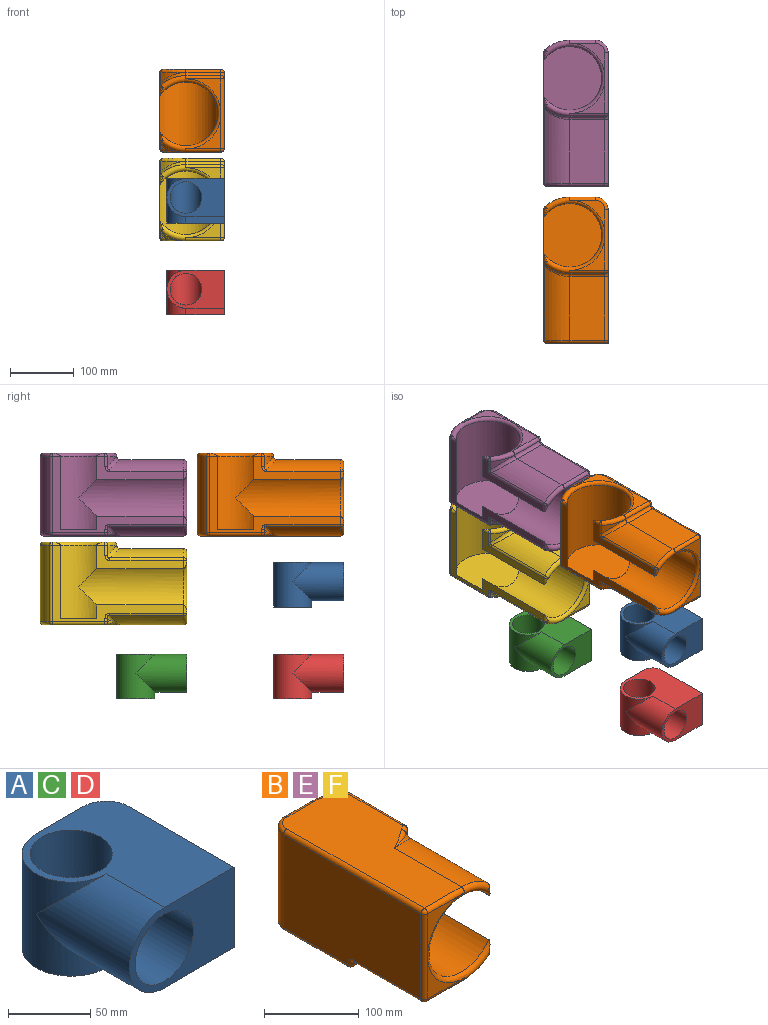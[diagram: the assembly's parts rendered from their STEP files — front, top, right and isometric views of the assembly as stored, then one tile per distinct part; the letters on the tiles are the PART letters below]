
ASSEMBLY  parts=6 mates=11
PART A: 12 faces, bbox 90x110x70 mm
  f0: cylinder r=30mm len=70mm, axis (0,0,-1), area 4797.3mm2, adj f1,f2,f3,f6,f7
  f1: cylinder r=30mm len=80mm, axis (0,1,0), area 5739.8mm2, adj f0,f2,f4,f5
  f2: plane 110x90mm, normal (0,0,1), area 5964.4mm2, adj f0,f1,f4,f7,f8,f9,f11
  f3: plane 90x60mm, normal (0,0,-1), area 2964.4mm2, adj f0,f6,f7,f8,f9,f11
  f4: plane 90x60mm, normal (0,-1,0), area 3050.2mm2, adj f1,f2,f5,f8,f10
  f5: plane 60x50mm, normal (0,0,-1), area 3000mm2, adj f1,f4,f6,f8
  f6: plane 60x10mm, normal (0,-1,0), area 600mm2, adj f0,f3,f5,f8
  f7: plane 70x40mm, normal (0,1,0), area 2800mm2, adj f0,f2,f3,f11
  f8: plane 90x70mm, normal (1,0,0), area 5800mm2, adj f2,f3,f4,f5,f6,f11
  f9: cylinder r=25mm len=70mm, axis (0,0,-1), area 8495.6mm2, adj f2,f3,f10
  f10: cylinder r=25mm len=80mm, axis (0,-1,0), area 10066.4mm2, adj f4,f9
  f11: cylinder r=20mm len=70mm, axis (0,0,-1), area 2199.1mm2, adj f2,f3,f7,f8
PART B: 61 faces, bbox 118.2x234.9x135 mm
  f0: plane 220x91mm, normal (0,0,1), area 15826.8mm2, adj f9,f38,f43,f44,f46,f49,f51,f52
  f1: plane 55x55mm, normal (0,0,-1), area 600.9mm2, adj f29,f30,f33,f60
  f2: plane 55x55mm, normal (0,0,-1), area 649.2mm2, adj f24,f29,f30
  f3: plane 55x55mm, normal (0,-1,0), area 649.2mm2, adj f34,f40,f44
  f4: cylinder r=60mm len=7.3mm, axis (0,0,-1), area 26.6mm2, adj f52,f53,f57
  f5: cylinder r=60mm len=39.27mm, axis (0,0,-1), area 339.5mm2, adj f21,f22,f29
  f6: cylinder r=60mm len=115.86mm, axis (0,1,0), area 4621mm2, adj f12,f21,f32,f40
  f7: cylinder r=50mm len=115mm, axis (0,0,-1), area 20203.4mm2, adj f15,f16,f17,f18,f29
  f8: cylinder r=60mm len=120mm, axis (0,0,-1), area 5137.8mm2, adj f13,f29,f45,f46
  f9: cylinder r=60mm len=115.86mm, axis (0,1,0), area 4621mm2, adj f0,f40,f53,f54
  f10: plane 55x55mm, normal (0,-1,0), area 649.2mm2, adj f34,f35,f40
  f11: plane 205x120mm, normal (-1,0,0), area 23521.5mm2, adj f20,f26,f30,f34,f38,f59
  f12: plane 100x55mm, normal (0,0,-1), area 5500mm2, adj f6,f19,f26,f35
  f13: plane 120x40mm, normal (0,1,0), area 4800mm2, adj f8,f33,f43,f59
  f14: cylinder r=50mm len=41mm, axis (0,0,-1), area 513.9mm2, adj f15,f16,f18
  f15: plane 100x91mm, normal (0,0,-1), area 7503.9mm2, adj f7,f14,f18
  f16: cylinder r=50mm len=165mm, axis (0,-1,0), area 33378.3mm2, adj f7,f14,f17,f18,f40
  f17: plane 136.38x36.38mm, normal (1,0,0), area 2082.1mm2, adj f7,f16,f22,f27,f28,f32,f41
  f18: plane 206.58x120mm, normal (1,0,0), area 3794.2mm2, adj f7,f14,f15,f16,f37,f45,f47,f51
  f19: cylinder r=5mm len=55mm, axis (-1,0,0), area 432mm2, adj f12,f20,f21,f24
  f20: torus R=10mm, axis (-1,0,0), area 84.1mm2, adj f11,f19,f25,f26
  f21: bspline ~51.65x23.96mm, area 321.1mm2, adj f5,f6,f19,f27
  f22: cylinder r=5mm len=15.86mm, axis (0,0,-1), area 68mm2, adj f5,f17,f23,f27
  f23: sphere r=5mm, area 13.6mm2, adj f22,f28,f29
  f24: cylinder r=5mm len=55mm, axis (-1,0,0), area 432mm2, adj f2,f19,f25,f29
  f25: sphere r=5mm, area 39.3mm2, adj f20,f24,f30
  f26: cylinder r=5mm len=100mm, axis (0,-1,0), area 785.4mm2, adj f11,f12,f20,f31
  f27: bspline ~9.27x8.4mm, area 34.5mm2, adj f17,f21,f22,f32
  f28: cylinder r=5mm len=12.96mm, axis (0,1,0), area 50.9mm2, adj f17,f23,f29
  f29: torus R=55mm, axis (0,0,1), area 2610.7mm2, adj f1,f2,f5,f7,f8,f23,f24,f28
  f30: cylinder r=5mm len=95mm, axis (0,-1,0), area 746.1mm2, adj f1,f2,f11,f25,f60
  f31: sphere r=5mm, area 25mm2, adj f26,f34,f35
  f32: cylinder r=5mm len=115.86mm, axis (0,1,0), area 496.6mm2, adj f6,f17,f27,f36
  f33: cylinder r=5mm len=40mm, axis (-1,0,0), area 314.2mm2, adj f1,f13,f29,f60
  f34: cylinder r=5mm len=110mm, axis (0,0,1), area 863.9mm2, adj f3,f10,f11,f31,f39
  f35: cylinder r=5mm len=55mm, axis (1,0,0), area 432mm2, adj f10,f12,f31,f40
  f36: sphere r=5mm, area 27.9mm2, adj f32,f40,f41
  f37: cylinder r=5mm len=12.96mm, axis (0,1,0), area 50.9mm2, adj f18,f29,f42
  f38: cylinder r=5mm len=205mm, axis (0,1,0), area 1610.1mm2, adj f0,f11,f39,f58
  f39: sphere r=5mm, area 53.5mm2, adj f34,f38,f44
  f40: torus R=55mm, axis (0,-1,0), area 2610.7mm2, adj f3,f6,f9,f10,f16,f35,f36,f41
  f41: cylinder r=5mm len=12.96mm, axis (0,0,-1), area 50.9mm2, adj f17,f36,f40
  f42: sphere r=5mm, area 21.4mm2, adj f29,f37,f45
  f43: cylinder r=5mm len=40mm, axis (1,0,0), area 314.2mm2, adj f0,f13,f46,f58
  f44: cylinder r=5mm len=55mm, axis (1,0,0), area 432mm2, adj f0,f3,f39,f40
  f45: cylinder r=5mm len=120mm, axis (0,0,-1), area 514.3mm2, adj f8,f18,f42,f48
  f46: torus R=55mm, axis (0,0,1), area 326.1mm2, adj f0,f8,f43,f48
  f47: cylinder r=5mm len=12.96mm, axis (0,0,-1), area 50.9mm2, adj f18,f40,f50
  f48: sphere r=5mm, area 21.4mm2, adj f45,f46,f51
  f49: bspline ~35.02x20.17mm, area 89.6mm2, adj f0,f52,f53
  f50: sphere r=5mm, area 21.4mm2, adj f40,f47,f54
  f51: cylinder r=5mm len=83.16mm, axis (0,-1,0), area 653.2mm2, adj f0,f18,f48,f55
  f52: torus R=55mm, axis (0,0,1), area 69.2mm2, adj f0,f4,f49,f55
  f53: bspline ~45.78x23.96mm, area 192mm2, adj f4,f9,f49,f56
  f54: cylinder r=5mm len=115.86mm, axis (0,1,0), area 496.6mm2, adj f9,f18,f50,f56
  f55: sphere r=5mm, area 21.4mm2, adj f51,f52,f57
  f56: bspline ~9.27x8.4mm, area 34.5mm2, adj f18,f53,f54,f57
  f57: cylinder r=5mm len=5.86mm, axis (0,0,-1), area 25.1mm2, adj f4,f18,f55,f56
  f58: torus R=15mm, axis (0,0,1), area 224.3mm2, adj f0,f38,f43,f59
  f59: cylinder r=20mm len=120mm, axis (0,0,-1), area 3769.9mm2, adj f11,f13,f58,f60
  f60: torus R=15mm, axis (0,0,1), area 224.3mm2, adj f1,f30,f33,f59
PART C: same geometry as A
PART D: same geometry as A
PART E: same geometry as B
PART F: same geometry as B
PLACE A rot(axis=(-0.07,-0.3,-0.95),0deg) t=(344.34,-371.74,253.96)mm
PLACE B rot(axis=(0,1,0),180deg) t=(262.34,-281.74,385.51)mm
PLACE C rot(axis=(-0.07,-0.3,-0.95),0deg) t=(344.34,-125.03,109.89)mm
PLACE D rot(axis=(-0.07,-0.3,-0.95),0deg) t=(344.34,-371.74,109.89)mm
PLACE E rot(axis=(0,1,0),180deg) t=(262.34,-35.03,385.51)mm
PLACE F rot(axis=(0,1,0),180deg) t=(262.34,-35.03,245.75)mm
MATE planar F.f11 <-> C.f8  axis (1,0,0) through (404.34,-95.3,248.22)mm
MATE planar B.f11 <-> D.f8  axis (1,0,0) through (404.34,-342.02,387.99)mm
MATE planar C.f5 <-> D.f5  axis (0,0,-1) through (374.34,-180.03,79.89)mm
MATE planar B.f11 <-> A.f8  axis (1,0,0) through (404.34,-342.02,387.99)mm
MATE planar D.f4 <-> B.f3  axis (0,-1,0) through (373.85,-451.74,109.89)mm
MATE planar A.f4 <-> B.f10  axis (0,-1,0) through (373.85,-451.74,253.96)mm
MATE planar E.f11 <-> C.f8  axis (1,0,0) through (404.34,-95.3,387.99)mm
MATE planar C.f4 <-> E.f3  axis (0,-1,0) through (373.85,-205.03,109.89)mm
MATE planar B.f12 <-> E.f12  axis (0,0,1) through (371.84,-396.74,445.51)mm
MATE planar B.f11 <-> E.f11  axis (1,0,0) through (404.34,-342.02,387.99)mm
MATE planar E.f13 <-> F.f13  axis (0,1,0) through (364.34,24.97,390.51)mm
